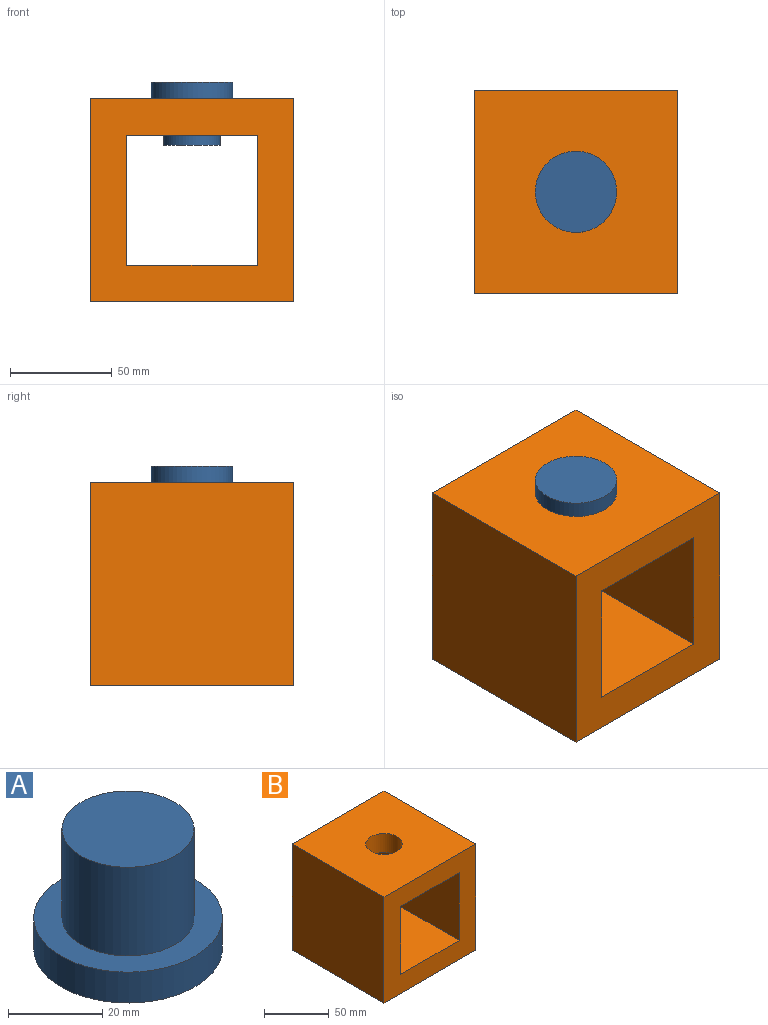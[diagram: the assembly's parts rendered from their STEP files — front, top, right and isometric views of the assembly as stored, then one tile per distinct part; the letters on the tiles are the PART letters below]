
ASSEMBLY  parts=2 mates=1
PART A: 5 faces, bbox 40x40x31 mm
  f0: cylinder r=20mm len=40mm, axis (0,0,-1), area 1005.3mm2, adj f1,f2
  f1: plane 40x40mm, normal (0,0,1), area 640.9mm2, adj f0,f3
  f2: plane 40x40mm, normal (0,0,-1), area 1256.6mm2, adj f0
  f3: cylinder r=14mm len=28mm, axis (0,0,-1), area 2023.2mm2, adj f1,f4
  f4: plane 28x28mm, normal (0,0,1), area 615.8mm2, adj f3
PART B: 11 faces, bbox 100x100x100 mm
  f0: plane 100x64mm, normal (0,0,1), area 6400mm2, adj f1,f3,f6,f7
  f1: plane 100x100mm, normal (0,-1,0), area 5904mm2, adj f0,f2,f4,f5,f6,f7,f8,f9
  f2: plane 100x100mm, normal (1,0,0), area 10000mm2, adj f1,f3,f5,f8
  f3: plane 100x100mm, normal (0,1,0), area 5904mm2, adj f0,f2,f4,f5,f6,f7,f8,f9
  f4: plane 100x100mm, normal (-1,0,0), area 10000mm2, adj f1,f3,f5,f8
  f5: plane 100x100mm, normal (0,0,-1), area 10000mm2, adj f1,f2,f3,f4
  f6: plane 100x64mm, normal (1,0,0), area 6400mm2, adj f0,f1,f3,f9
  f7: plane 100x64mm, normal (-1,0,0), area 6400mm2, adj f0,f1,f3,f9
  f8: plane 100x100mm, normal (0,0,1), area 9384.2mm2, adj f1,f2,f3,f4,f10
  f9: plane 100x64mm, normal (0,0,-1), area 5784.2mm2, adj f1,f3,f6,f7,f10
  f10: cylinder r=14mm len=28mm, axis (0,0,1), area 1583.4mm2, adj f8,f9
PLACE A rot(axis=(0,1,0),180deg) t=(0,0,108)mm
PLACE B at identity
MATE slider A.f3 <-> B.f10  axis (0,0,1) through (0,0,100)mm
